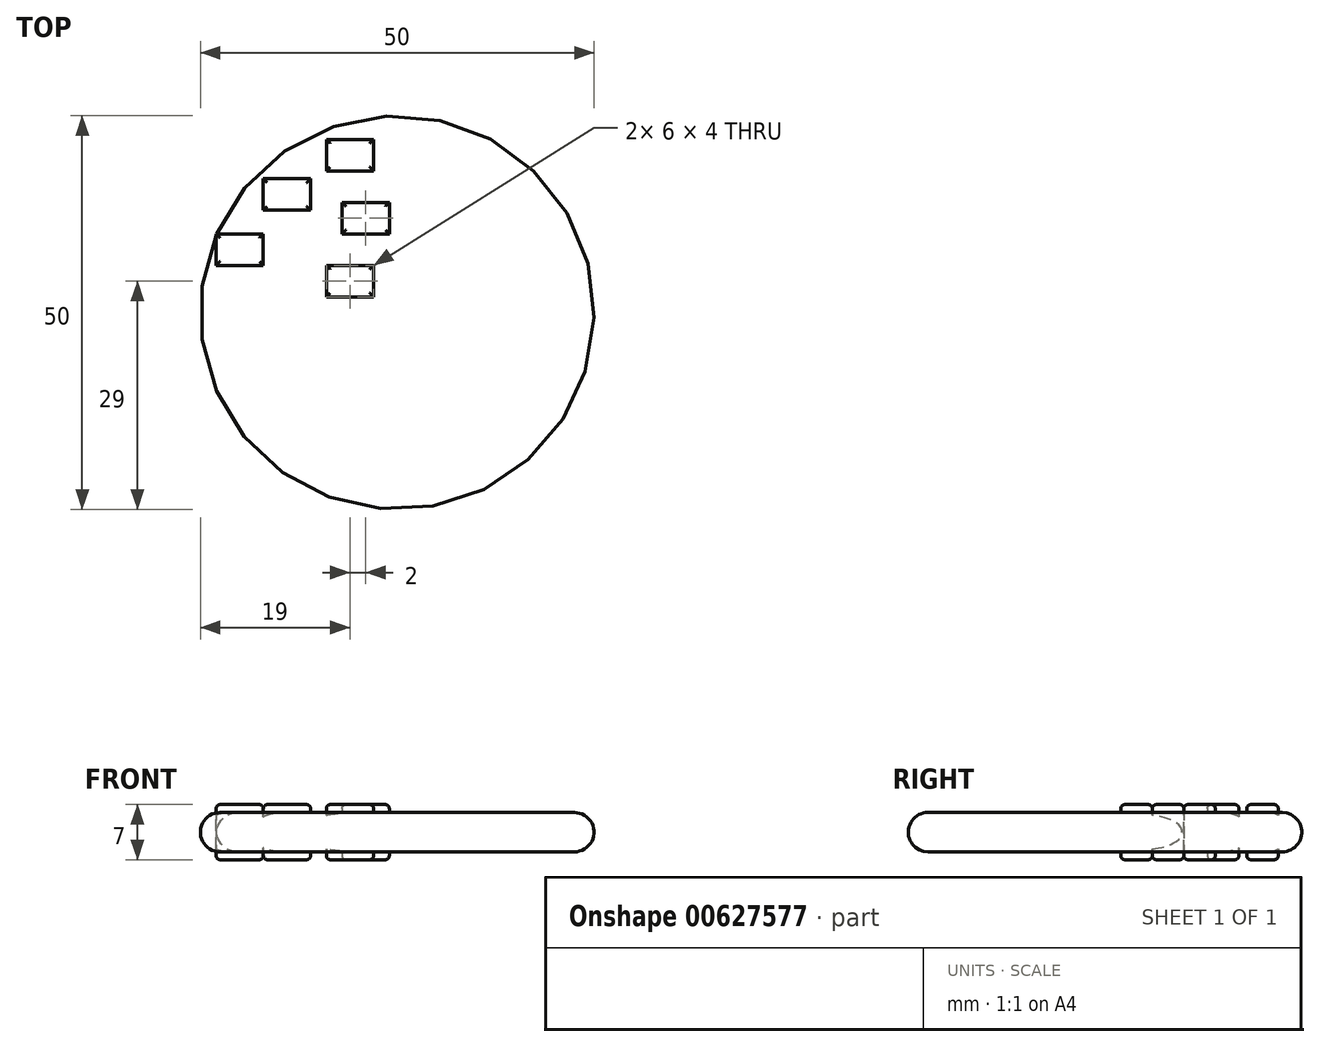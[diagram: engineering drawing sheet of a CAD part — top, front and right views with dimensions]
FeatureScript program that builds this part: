
annotation { "Feature Type Name" : "Feature", "Feature Type Description" : "" }
export const myFeature = defineFeature(function(context is Context, id is Id, definition is map)
    precondition{}
    {
        {
            var Q0;
            Q0=qCreatedBy(makeId("Top.planeOp"),FACE);
            var sketch = newSketch(context, id + "F0", { "sketchPlane" : qUnion([Q0])});
            skCircle(sketch, "E0", {"center": v(0, 0) * mm, "radius": 25 * mm});
            skSolve(sketch);
        }
        {
            var Q0;
            Q0=makeQuery(id+"F0.imprint","IMPRINT",FACE,{"disambiguationData":[TD([[makeQuery(id+"F0.imprint","IMPRINT",EDGE,{"derivedFrom":sQuery(id+"F0.wireOp",EDGE,"E0")}),1.0]])]});
            extrude(context, id + "F1", {"entities" : qUnion([Q0]), "depth" : 5 * mm, "offsetDistance" : 25 * mm});
        }
        {
            var Q0;
            Q0=makeQuery(id+"F1.opExtrude","CAP_EDGE",EDGE,{"disambiguationData":[OSD([sQuery(id+"F0.wireOp",EDGE,"E0")])],"isStart":false});
            var Q1;
            Q1=makeQuery(id+"F1.opExtrude","CAP_EDGE",EDGE,{"disambiguationData":[OSD([sQuery(id+"F0.wireOp",EDGE,"E0")])],"isStart":true});
            fillet(context, id + "F2", {"entities" : qUnion([Q0, Q1]), "radius" : 2.5 * mm, "tangentPropagation" : true, "allowEdgeOverflow" : false});
        }
        {
            var Q0;
            Q0=qCreatedBy(makeId("Top.planeOp"),FACE);
            var sketch = newSketch(context, id + "F3", { "sketchPlane" : qUnion([Q0])});
            skLineSegment(sketch, "E1.bottom", {"start": v(-17, 6) * mm, "end": v(-23, 6) * mm});
            skLineSegment(sketch, "E1.top", {"start": v(-17, 10) * mm, "end": v(-23, 10) * mm});
            skLineSegment(sketch, "E1.left", {"start": v(-17, 6) * mm, "end": v(-17, 10) * mm});
            skLineSegment(sketch, "E1.right", {"start": v(-23, 6) * mm, "end": v(-23, 10) * mm});
            skPoint(sketch, "E1.middle", {"position": v(-20, 8) * mm});
            skLineSegment(sketch, "E2.bottom", {"start": v(-11, 13) * mm, "end": v(-17, 13) * mm});
            skLineSegment(sketch, "E2.top", {"start": v(-11, 17) * mm, "end": v(-17, 17) * mm});
            skLineSegment(sketch, "E2.left", {"start": v(-11, 13) * mm, "end": v(-11, 17) * mm});
            skLineSegment(sketch, "E2.right", {"start": v(-17, 13) * mm, "end": v(-17, 17) * mm});
            skPoint(sketch, "E2.middle", {"position": v(-14, 15) * mm});
            skLineSegment(sketch, "E3.bottom", {"start": v(-1, 10) * mm, "end": v(-7, 10) * mm});
            skLineSegment(sketch, "E3.top", {"start": v(-1, 14) * mm, "end": v(-7, 14) * mm});
            skLineSegment(sketch, "E3.left", {"start": v(-1, 10) * mm, "end": v(-1, 14) * mm});
            skLineSegment(sketch, "E3.right", {"start": v(-7, 10) * mm, "end": v(-7, 14) * mm});
            skPoint(sketch, "E3.middle", {"position": v(-4, 12) * mm});
            skLineSegment(sketch, "E4.bottom", {"start": v(-3, 2) * mm, "end": v(-9, 2) * mm});
            skLineSegment(sketch, "E4.top", {"start": v(-3, 6) * mm, "end": v(-9, 6) * mm});
            skLineSegment(sketch, "E4.left", {"start": v(-3, 2) * mm, "end": v(-3, 6) * mm});
            skLineSegment(sketch, "E4.right", {"start": v(-9, 2) * mm, "end": v(-9, 6) * mm});
            skPoint(sketch, "E4.middle", {"position": v(-6, 4) * mm});
            skLineSegment(sketch, "E5.bottom", {"start": v(-3, 18) * mm, "end": v(-9, 18) * mm});
            skLineSegment(sketch, "E5.top", {"start": v(-3, 22) * mm, "end": v(-9, 22) * mm});
            skLineSegment(sketch, "E5.left", {"start": v(-3, 18) * mm, "end": v(-3, 22) * mm});
            skLineSegment(sketch, "E5.right", {"start": v(-9, 18) * mm, "end": v(-9, 22) * mm});
            skPoint(sketch, "E5.middle", {"position": v(-6, 20) * mm});
            skSolve(sketch);
        }
        {
            var Q0;
            Q0 = qSketchRegion(id + "F3", true);
            extrude(context, id + "F4", {"entities" : qUnion([Q0]), "operationType" : NewBodyOperationType.ADD, "depth" : 6 * mm, "offsetDistance" : 25 * mm, "hasSecondDirection" : true, "secondDirectionOppositeDirection" : true, "secondDirectionDepth" : 1 * mm});
        }
        {
            var Q0;
            Q0=makeQuery(id+"F4.opExtrude","CAP_FACE",FACE,{"disambiguationData":[OSD([sQuery(id+"F3.wireOp",EDGE,"E4.bottom"),sQuery(id+"F3.wireOp",EDGE,"E4.top"),sQuery(id+"F3.wireOp",EDGE,"E4.left"),sQuery(id+"F3.wireOp",EDGE,"E4.right")])],"isStart":false});
            var Q1;
            Q1=makeQuery(id+"F4.opExtrude","CAP_FACE",FACE,{"disambiguationData":[OSD([sQuery(id+"F3.wireOp",EDGE,"E3.bottom"),sQuery(id+"F3.wireOp",EDGE,"E3.top"),sQuery(id+"F3.wireOp",EDGE,"E3.left"),sQuery(id+"F3.wireOp",EDGE,"E3.right")])],"isStart":false});
            var Q2;
            Q2=makeQuery(id+"F4.opExtrude","CAP_FACE",FACE,{"disambiguationData":[OSD([sQuery(id+"F3.wireOp",EDGE,"E2.bottom"),sQuery(id+"F3.wireOp",EDGE,"E2.top"),sQuery(id+"F3.wireOp",EDGE,"E2.left"),sQuery(id+"F3.wireOp",EDGE,"E2.right")])],"isStart":false});
            var Q3;
            Q3=makeQuery(id+"F4.opExtrude","CAP_FACE",FACE,{"disambiguationData":[OSD([sQuery(id+"F3.wireOp",EDGE,"E5.bottom"),sQuery(id+"F3.wireOp",EDGE,"E5.top"),sQuery(id+"F3.wireOp",EDGE,"E5.left"),sQuery(id+"F3.wireOp",EDGE,"E5.right")])],"isStart":false});
            var Q4;
            Q4=makeQuery(id+"F4.opExtrude","CAP_FACE",FACE,{"disambiguationData":[OSD([sQuery(id+"F3.wireOp",EDGE,"E1.bottom"),sQuery(id+"F3.wireOp",EDGE,"E1.top"),sQuery(id+"F3.wireOp",EDGE,"E1.left"),sQuery(id+"F3.wireOp",EDGE,"E1.right")])],"isStart":false});
            var Q5;
            Q5=makeQuery(id+"F4.opExtrude","CAP_FACE",FACE,{"disambiguationData":[OSD([sQuery(id+"F3.wireOp",EDGE,"E1.bottom"),sQuery(id+"F3.wireOp",EDGE,"E1.top"),sQuery(id+"F3.wireOp",EDGE,"E1.left"),sQuery(id+"F3.wireOp",EDGE,"E1.right")])],"isStart":true});
            var Q6;
            Q6=makeQuery(id+"F4.opExtrude","CAP_FACE",FACE,{"disambiguationData":[OSD([sQuery(id+"F3.wireOp",EDGE,"E4.bottom"),sQuery(id+"F3.wireOp",EDGE,"E4.top"),sQuery(id+"F3.wireOp",EDGE,"E4.left"),sQuery(id+"F3.wireOp",EDGE,"E4.right")])],"isStart":true});
            var Q7;
            Q7=makeQuery(id+"F4.opExtrude","CAP_FACE",FACE,{"disambiguationData":[OSD([sQuery(id+"F3.wireOp",EDGE,"E3.bottom"),sQuery(id+"F3.wireOp",EDGE,"E3.top"),sQuery(id+"F3.wireOp",EDGE,"E3.left"),sQuery(id+"F3.wireOp",EDGE,"E3.right")])],"isStart":true});
            var Q8;
            Q8=makeQuery(id+"F4.opExtrude","CAP_FACE",FACE,{"disambiguationData":[OSD([sQuery(id+"F3.wireOp",EDGE,"E2.bottom"),sQuery(id+"F3.wireOp",EDGE,"E2.top"),sQuery(id+"F3.wireOp",EDGE,"E2.left"),sQuery(id+"F3.wireOp",EDGE,"E2.right")])],"isStart":true});
            var Q9;
            Q9=makeQuery(id+"F4.opExtrude","CAP_FACE",FACE,{"disambiguationData":[OSD([sQuery(id+"F3.wireOp",EDGE,"E5.bottom"),sQuery(id+"F3.wireOp",EDGE,"E5.top"),sQuery(id+"F3.wireOp",EDGE,"E5.left"),sQuery(id+"F3.wireOp",EDGE,"E5.right")])],"isStart":true});
            fillet(context, id + "F5", {"entities" : qUnion([Q0, Q1, Q2, Q3, Q4, Q5, Q6, Q7, Q8, Q9]), "radius" : 0.5 * mm, "tangentPropagation" : true, "allowEdgeOverflow" : false});
        }
        {
            var Q0;
            Q0=qCreatedBy(makeId("Right.planeOp"),FACE);
            var sketch = newSketch(context, id + "F6", { "sketchPlane" : qUnion([Q0])});
            skLineSegment(sketch, "E6", {"start": v(0, -14.9) * mm, "end": v(0, 40.14) * mm, "construction": true});
            skSolve(sketch);
        }
    });
